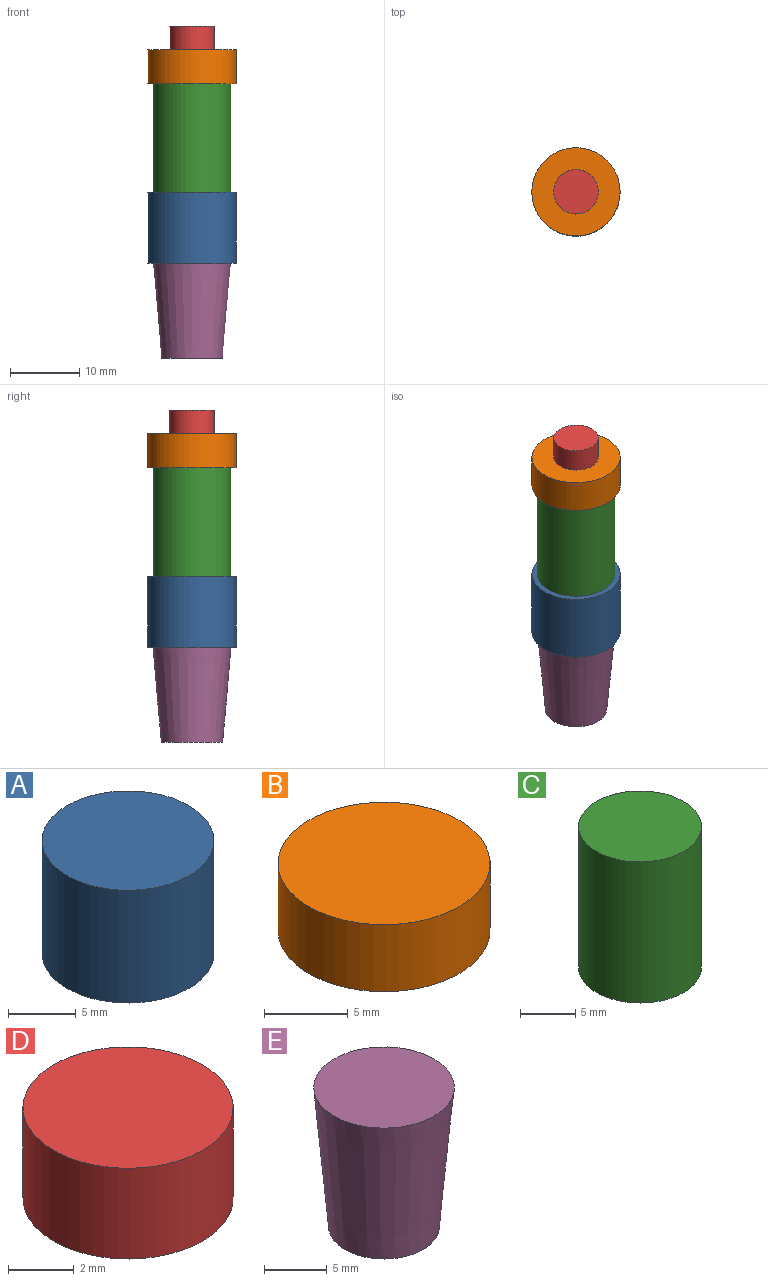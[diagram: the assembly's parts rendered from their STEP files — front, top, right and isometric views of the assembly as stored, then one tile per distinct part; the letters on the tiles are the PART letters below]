
ASSEMBLY  parts=5 mates=4
PART A: 3 faces, bbox 12.7x12.7x10.2 mm
  f0: cylinder r=6.35mm len=12.7mm, axis (0,0,-1), area 406.4mm2, adj f1,f2
  f1: plane 12.7x12.7mm, normal (0,0,1), area 126.7mm2, adj f0
  f2: plane 12.7x12.7mm, normal (0,0,-1), area 126.7mm2, adj f0
PART B: 3 faces, bbox 12.7x12.7x4.9 mm
  f0: cylinder r=6.35mm len=12.7mm, axis (0,0,-1), area 196mm2, adj f1,f2
  f1: plane 12.7x12.7mm, normal (0,0,1), area 126.7mm2, adj f0
  f2: plane 12.7x12.7mm, normal (0,0,-1), area 126.7mm2, adj f0
PART C: 3 faces, bbox 11.2x11.2x15.7 mm
  f0: cylinder r=5.58mm len=15.66mm, axis (0,0,-1), area 548.7mm2, adj f1,f2
  f1: plane 11.15x11.15mm, normal (0,0,1), area 97.7mm2, adj f0
  f2: plane 11.15x11.15mm, normal (0,0,-1), area 97.7mm2, adj f0
PART D: 3 faces, bbox 6.4x6.4x3.4 mm
  f0: cylinder r=3.2mm len=6.4mm, axis (0,0,-1), area 68mm2, adj f1,f2
  f1: plane 6.4x6.4mm, normal (0,0,1), area 32.2mm2, adj f0
  f2: plane 6.4x6.4mm, normal (0,0,-1), area 32.2mm2, adj f0
PART E: 3 faces, bbox 11.2x11.2x13.6 mm
  f0: cone r=4.42mm half-angle=5deg, axis (0,0,1), area 431.5mm2, adj f1,f2
  f1: plane 11.23x11.23mm, normal (0,0,1), area 99mm2, adj f0
  f2: plane 8.84x8.84mm, normal (0,0,-1), area 61.4mm2, adj f0
PLACE A t=(-127.94,8.36,-188.35)mm
PLACE B t=(-127.94,8.36,-162.5)mm
PLACE C t=(-127.94,8.36,-178.16)mm
PLACE D t=(-128.64,6.65,-157.59)mm
PLACE E rot(axis=(0,0,1),90deg) t=(-127.94,8.36,-201.99)mm
MATE fastened A.f0 <-> C.f0  axis (0,0,1) through (-127.94,8.36,-178.16)mm
MATE fastened D.f0 <-> B.f0  axis (0,0,-1) through (-127.94,8.36,-157.59)mm
MATE planar A.f0 <-> A.f0  axis (0,0,1) through (-127.94,8.36,-178.16)mm
MATE fastened E.f0 <-> A.f0  axis (0,0,1) through (-127.94,8.36,-188.35)mm
